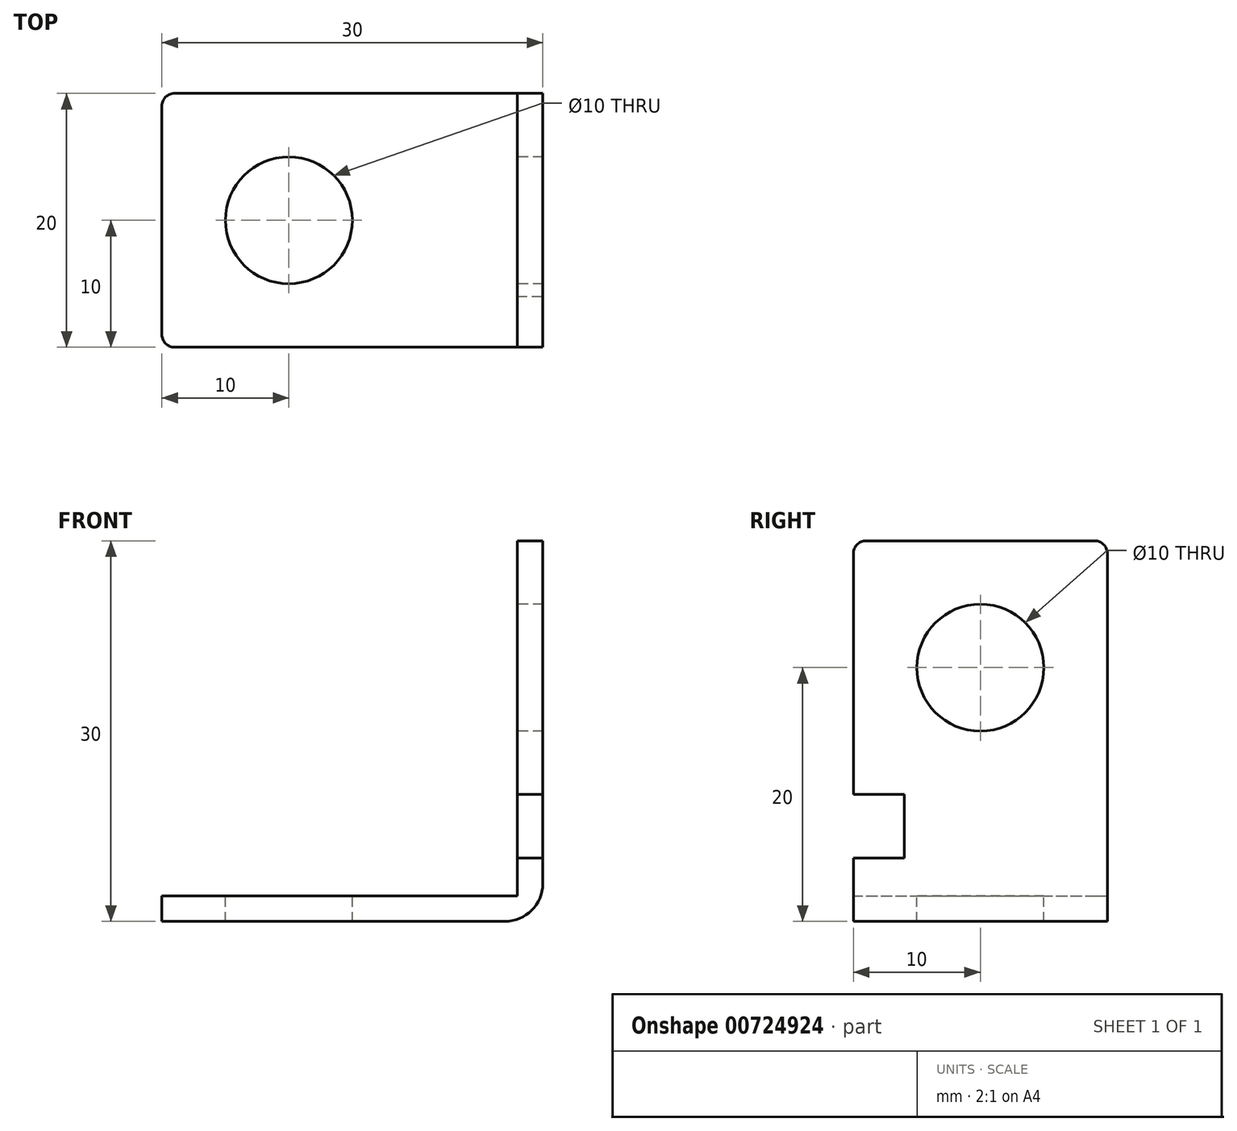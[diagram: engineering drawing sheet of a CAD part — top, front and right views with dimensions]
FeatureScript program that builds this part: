
annotation { "Feature Type Name" : "Feature", "Feature Type Description" : "" }
export const myFeature = defineFeature(function(context is Context, id is Id, definition is map)
    precondition{}
    {
        {
            var Q0;
            Q0=qCreatedBy(makeId("Front.planeOp"),FACE);
            var sketch = newSketch(context, id + "F0", { "sketchPlane" : qUnion([Q0])});
            skLineSegment(sketch, "E0", {"start": v(0, 0) * mm, "end": v(27, 0) * mm});
            skLineSegment(sketch, "E1", {"start": v(30, 3) * mm, "end": v(30, 30) * mm});
            skLineSegment(sketch, "E2", {"start": v(30, 30) * mm, "end": v(28, 30) * mm});
            skLineSegment(sketch, "E3", {"start": v(28, 30) * mm, "end": v(28, 2) * mm});
            skLineSegment(sketch, "E4", {"start": v(28, 2) * mm, "end": v(0, 2) * mm});
            skLineSegment(sketch, "E5", {"start": v(0, 2) * mm, "end": v(0, 0) * mm});
            skPoint(sketch, "E6.visualSharp", {"position": v(30, 0) * mm});
            skArc(sketch, "E6.filletArc", {"start": v(27, 0) * mm, "mid": v(29.12, 0.88) * mm, "end": v(30, 3) * mm});
            skSolve(sketch);
        }
        {
            var Q0;
            Q0 = qSketchRegion(id + "F0", true);
            extrude(context, id + "F1", {"entities" : qUnion([Q0]), "depth" : 20 * mm, "offsetDistance" : 25 * mm});
        }
        {
            var Q0;
            Q0=makeQuery(id+"F1.opExtrude","SWEPT_FACE",FACE,{"disambiguationData":[OSD([sQuery(id+"F0.wireOp",EDGE,"E3")])]});
            var sketch = newSketch(context, id + "F2", { "sketchPlane" : qUnion([Q0])});
            skCircle(sketch, "E7", {"center": v(10, 20) * mm, "radius": 5 * mm});
            skSolve(sketch);
        }
        {
            var Q0;
            Q0 = qSketchRegion(id + "F2", true);
            extrude(context, id + "F3", {"entities" : qUnion([Q0]), "operationType" : NewBodyOperationType.REMOVE, "endBound" : BoundingType.THROUGH_ALL, "oppositeDirection" : true, "depth" : 25 * mm, "offsetDistance" : 25 * mm});
        }
        {
            var Q0;
            Q0=makeQuery(id+"F1.opExtrude","SWEPT_FACE",FACE,{"disambiguationData":[OSD([sQuery(id+"F0.wireOp",EDGE,"E4")])]});
            var sketch = newSketch(context, id + "F4", { "sketchPlane" : qUnion([Q0])});
            skCircle(sketch, "E8", {"center": v(10, -10) * mm, "radius": 5 * mm});
            skSolve(sketch);
        }
        {
            var Q0;
            Q0 = qSketchRegion(id + "F4", true);
            extrude(context, id + "F5", {"entities" : qUnion([Q0]), "operationType" : NewBodyOperationType.REMOVE, "endBound" : BoundingType.THROUGH_ALL, "oppositeDirection" : true, "depth" : 25 * mm, "offsetDistance" : 25 * mm});
        }
        {
            var Q0;
            Q0=makeQuery(id+"F1.opExtrude","SWEPT_FACE",FACE,{"disambiguationData":[OSD([sQuery(id+"F0.wireOp",EDGE,"E1")])]});
            var sketch = newSketch(context, id + "F6", { "sketchPlane" : qUnion([Q0])});
            skLineSegment(sketch, "E9.bottom", {"start": v(-20, 10) * mm, "end": v(-16, 10) * mm});
            skLineSegment(sketch, "E9.top", {"start": v(-20, 5) * mm, "end": v(-16, 5) * mm});
            skLineSegment(sketch, "E9.left", {"start": v(-20, 10) * mm, "end": v(-20, 5) * mm});
            skLineSegment(sketch, "E9.right", {"start": v(-16, 10) * mm, "end": v(-16, 5) * mm});
            skSolve(sketch);
        }
        {
            var Q0;
            Q0 = qSketchRegion(id + "F6", true);
            extrude(context, id + "F7", {"entities" : qUnion([Q0]), "operationType" : NewBodyOperationType.REMOVE, "endBound" : BoundingType.THROUGH_ALL, "oppositeDirection" : true, "depth" : 25 * mm, "offsetDistance" : 25 * mm});
        }
        {
            var Q0;
            Q0=makeQuery(id+"F1.opExtrude","CAP_EDGE",EDGE,{"disambiguationData":[OSD([sQuery(id+"F0.wireOp",EDGE,"E5")])],"isStart":false});
            var Q1;
            Q1=makeQuery(id+"F1.opExtrude","CAP_EDGE",EDGE,{"disambiguationData":[OSD([sQuery(id+"F0.wireOp",EDGE,"E5")])],"isStart":true});
            var Q2;
            Q2=makeQuery(id+"F1.opExtrude","CAP_EDGE",EDGE,{"disambiguationData":[OSD([sQuery(id+"F0.wireOp",EDGE,"E2")])],"isStart":true});
            var Q3;
            Q3=makeQuery(id+"F1.opExtrude","CAP_EDGE",EDGE,{"disambiguationData":[OSD([sQuery(id+"F0.wireOp",EDGE,"E2")])],"isStart":false});
            fillet(context, id + "F8", {"entities" : qUnion([Q0, Q1, Q2, Q3]), "radius" : 1 * mm, "tangentPropagation" : true, "allowEdgeOverflow" : false});
        }
    });
